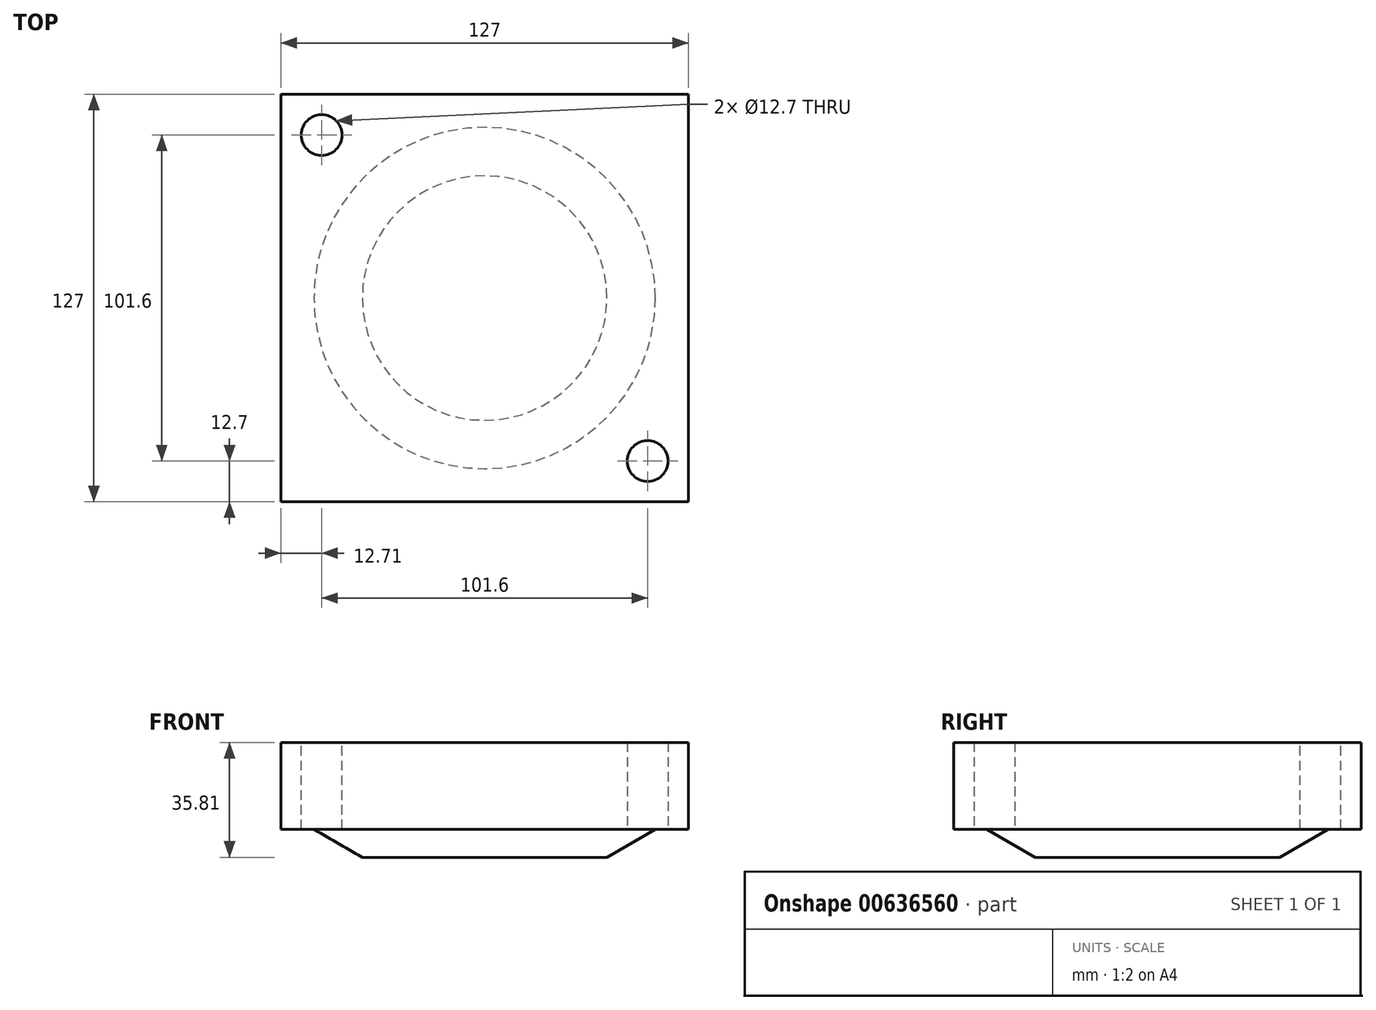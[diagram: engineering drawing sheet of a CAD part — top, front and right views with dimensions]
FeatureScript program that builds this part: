
annotation { "Feature Type Name" : "Feature", "Feature Type Description" : "" }
export const myFeature = defineFeature(function(context is Context, id is Id, definition is map)
    precondition{}
    {
        {
            var Q0;
            Q0=qCreatedBy(makeId("Front.planeOp"),FACE);
            var sketch = newSketch(context, id + "F0", { "sketchPlane" : qUnion([Q0])});
            skLineSegment(sketch, "E0", {"start": v(38.1, 2.29) * mm, "end": v(0, 2.29) * mm});
            skLineSegment(sketch, "E1", {"start": v(0, 2.29) * mm, "end": v(0, 0) * mm});
            skLineSegment(sketch, "E2", {"start": v(38.1, 2.29) * mm, "end": v(53.2, 11) * mm});
            skPoint(sketch, "E3.middle", {"position": v(0, 2.29) * mm});
            skLineSegment(sketch, "E4", {"start": v(0, 2.29) * mm, "end": v(38.1, 2.29) * mm});
            skLineSegment(sketch, "E5", {"start": v(53.2, 11) * mm, "end": v(132, 11) * mm});
            skLineSegment(sketch, "E6", {"start": v(132, 11) * mm, "end": v(132, 0) * mm});
            skLineSegment(sketch, "E7", {"start": v(0, 0) * mm, "end": v(132, 0) * mm});
            skSolve(sketch);
        }
        {
            var Q0;
            Q0=qCreatedBy(makeId("Front.planeOp"),FACE);
            var sketch = newSketch(context, id + "F1", { "sketchPlane" : qUnion([Q0])});
            skLineSegment(sketch, "E8.bottom", {"start": v(-63.5, 0) * mm, "end": v(63.5, 0) * mm});
            skLineSegment(sketch, "E8.top", {"start": v(-63.5, 38.1) * mm, "end": v(63.5, 38.1) * mm});
            skLineSegment(sketch, "E8.left", {"start": v(-63.5, 0) * mm, "end": v(-63.5, 38.1) * mm});
            skLineSegment(sketch, "E8.right", {"start": v(63.5, 0) * mm, "end": v(63.5, 38.1) * mm});
            skSolve(sketch);
        }
        {
            var Q0;
            Q0=makeQuery(id+"F1.imprint","IMPRINT",FACE,{"disambiguationData":[TD([[makeQuery(id+"F1.imprint","IMPRINT",EDGE,{"derivedFrom":sQuery(id+"F1.wireOp",EDGE,"E8.bottom")}),1.0]])]});
            extrude(context, id + "F2", {"entities" : qUnion([Q0]), "endBound" : BoundingType.SYMMETRIC, "depth" : 127 * mm, "offsetDistance" : 25.4 * mm});
        }
        {
            var Q0;
            Q0=makeQuery(id+"F0.imprint","IMPRINT",FACE,{"disambiguationData":[TD([[makeQuery(id+"F0.imprint","IMPRINT",EDGE,{"derivedFrom":sQuery(id+"F0.wireOp",EDGE,"E1")}),1.0]])]});
            var Q1;
            Q1=sQuery(id+"F0.wireOp",EDGE,"E1");
            revolve(context, id + "F3", {"operationType" : NewBodyOperationType.REMOVE, "entities" : qUnion([Q0]), "axis" : qUnion([Q1]), "revolveType" : RevolveType.FULL, "oppositeDirection" : true});
        }
        {
            var Q0;
            Q0=qCreatedBy(makeId("Top.planeOp"),FACE);
            var sketch = newSketch(context, id + "F4", { "sketchPlane" : qUnion([Q0])});
            skLineSegment(sketch, "E9", {"start": v(-50.8, 50.8) * mm, "end": v(0, 50.8) * mm});
            skLineSegment(sketch, "E10", {"start": v(-50.8, 50.8) * mm, "end": v(-50.8, 0) * mm});
            skCircle(sketch, "E11", {"center": v(-50.8, 50.8) * mm, "radius": 6.35 * mm});
            skSolve(sketch);
        }
        {
            var Q0;
            Q0=qSketchRegion(id+"F4",true);
            extrude(context, id + "F5", {"entities" : qUnion([Q0]), "operationType" : NewBodyOperationType.REMOVE, "endBound" : BoundingType.SYMMETRIC, "oppositeDirection" : true, "depth" : 101.6 * mm, "offsetDistance" : 25.4 * mm});
        }
        {
            var Q0;
            Q0=qCreatedBy(makeId("Top.planeOp"),FACE);
            var sketch = newSketch(context, id + "F6", { "sketchPlane" : qUnion([Q0])});
            skLineSegment(sketch, "E12", {"start": v(0, -50.8) * mm, "end": v(50.8, -50.8) * mm});
            skLineSegment(sketch, "E13", {"start": v(50.8, -50.8) * mm, "end": v(50.8, 0) * mm});
            skCircle(sketch, "E14", {"center": v(50.8, -50.8) * mm, "radius": 6.35 * mm});
            skSolve(sketch);
        }
        {
            var Q0;
            Q0 = qSketchRegion(id + "F6", true);
            extrude(context, id + "F7", {"entities" : qUnion([Q0]), "operationType" : NewBodyOperationType.REMOVE, "endBound" : BoundingType.SYMMETRIC, "depth" : 101.6 * mm, "offsetDistance" : 25.4 * mm});
        }
    });
